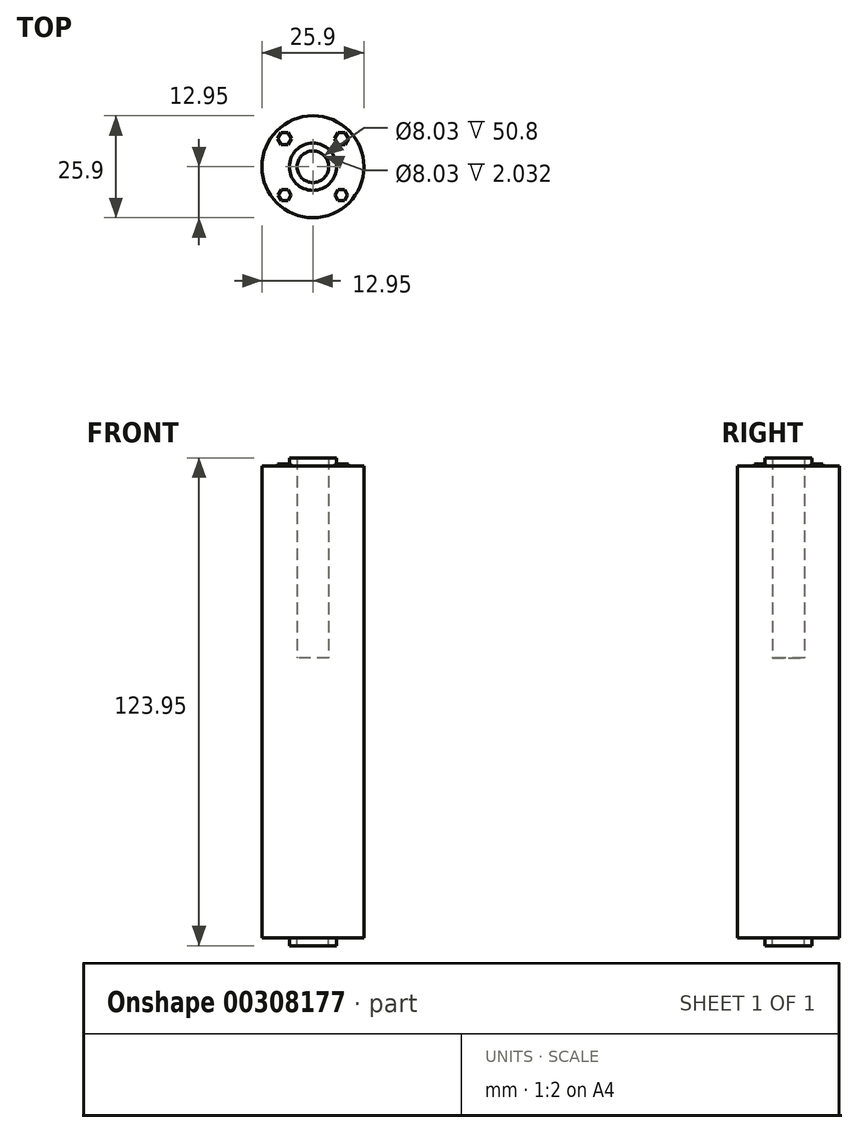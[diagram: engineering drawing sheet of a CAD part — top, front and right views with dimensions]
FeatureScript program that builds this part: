
annotation { "Feature Type Name" : "Feature", "Feature Type Description" : "" }
export const myFeature = defineFeature(function(context is Context, id is Id, definition is map)
    precondition{}
    {
        {
            var Q0;
            Q0=qCreatedBy(makeId("Top.planeOp"),FACE);
            var sketch = newSketch(context, id + "F0", { "sketchPlane" : qUnion([Q0])});
            skCircle(sketch, "E0", {"center": v(0, 0) * mm, "radius": 12.95 * mm});
            skCircle(sketch, "E1", {"center": v(0, 0) * mm, "radius": 6 * mm});
            skCircle(sketch, "E2", {"center": v(0, 0) * mm, "radius": 4.01 * mm});
            skSolve(sketch);
        }
        {
            var Q0;
            Q0 = qSketchRegion(id + "F0", true);
            var Q1;
            Q1=makeQuery(id+"F0.imprint","IMPRINT",FACE,{"disambiguationData":[TD([[makeQuery(id+"F0.imprint","IMPRINT",EDGE,{"derivedFrom":sQuery(id+"F0.wireOp",EDGE,"E1")}),1.0]])]});
            var Q2;
            Q2=makeQuery(id+"F0.imprint","IMPRINT",FACE,{"disambiguationData":[TD([[makeQuery(id+"F0.imprint","IMPRINT",EDGE,{"derivedFrom":sQuery(id+"F0.wireOp",EDGE,"E2")}),1.0]])]});
            extrude(context, id + "F1", {"entities" : qUnion([Q0, Q1, Q2]), "depth" : 119.89 * mm});
        }
        {
            var Q0;
            Q0=makeQuery(id+"F1.opExtrude","CAP_FACE",FACE,{"disambiguationData":[OSD([sQuery(id+"F0.wireOp",EDGE,"E0")])],"isStart":false});
            var sketch = newSketch(context, id + "F2", { "sketchPlane" : qUnion([Q0])});
            skCircle(sketch, "E3.0", {"center": v(0, 0) * mm, "radius": 4.01 * mm});
            skCircle(sketch, "E4.0", {"center": v(0, 0) * mm, "radius": 6 * mm});
            skSolve(sketch);
        }
        {
            var Q0;
            Q0=makeQuery(id+"F2.imprint","IMPRINT",FACE,{"disambiguationData":[TD([[makeQuery(id+"F2.imprint","IMPRINT",EDGE,{"derivedFrom":sQuery(id+"F2.wireOp",EDGE,"E3.0")}),-1.0]])]});
            extrude(context, id + "F3", {"entities" : qUnion([Q0]), "operationType" : NewBodyOperationType.ADD, "depth" : 2.03 * mm});
        }
        {
            var Q0;
            Q0=sQuery(id+"F0.wireOp",EDGE,"E2");
            var Q1;
            Q1=sQuery(id+"F0.wireOp",EDGE,"E1");
            extrude(context, id + "F4", {"bodyType" : ToolBodyType.SURFACE, "surfaceEntities" : qUnion([Q0, Q1]), "oppositeDirection" : true, "depth" : 2.03 * mm});
        }
        {
            var Q0;
            Q0=makeQuery(id+"F0.imprint","IMPRINT",FACE,{"disambiguationData":[TD([[makeQuery(id+"F0.imprint","IMPRINT",EDGE,{"derivedFrom":sQuery(id+"F0.wireOp",EDGE,"E2")}),1.0]])]});
            var sketch = newSketch(context, id + "F5", { "sketchPlane" : qUnion([Q0])});
            skCircle(sketch, "E5.0", {"center": v(0, 0) * mm, "radius": 4.01 * mm});
            skCircle(sketch, "E6.0", {"center": v(0, 0) * mm, "radius": 6 * mm});
            skSolve(sketch);
        }
        {
            var Q0;
            Q0 = qSketchRegion(id + "F5", true);
            var Q1;
            Q1=makeQuery(id+"F0.imprint","IMPRINT",FACE,{"disambiguationData":[TD([[makeQuery(id+"F0.imprint","IMPRINT",EDGE,{"derivedFrom":sQuery(id+"F0.wireOp",EDGE,"E1")}),1.0]])]});
            extrude(context, id + "F6", {"entities" : qUnion([Q0, Q1]), "operationType" : NewBodyOperationType.ADD, "oppositeDirection" : true, "depth" : 2.03 * mm});
        }
        {
            var Q0;
            Q0=makeQuery(id+"F3.opExtrude","CAP_FACE",FACE,{"disambiguationData":[OSD([sQuery(id+"F2.wireOp",EDGE,"E3.0"),sQuery(id+"F2.wireOp",EDGE,"E4.0")])],"isStart":false});
            var sketch = newSketch(context, id + "F7", { "sketchPlane" : qUnion([Q0])});
            skCircle(sketch, "E7.cCircle", {"center": v(0, 0) * mm, "radius": 6.99 * mm, "construction": true});
            skLineSegment(sketch, "E7.0", {"start": v(6.99, 6.99) * mm, "end": v(6.99, -6.99) * mm});
            skLineSegment(sketch, "E7.1", {"start": v(6.99, -6.99) * mm, "end": v(-6.99, -6.99) * mm});
            skLineSegment(sketch, "E7.2", {"start": v(-6.99, -6.99) * mm, "end": v(-6.99, 6.99) * mm});
            skLineSegment(sketch, "E7.3", {"start": v(-6.99, 6.99) * mm, "end": v(6.99, 6.99) * mm});
            skPoint(sketch, "E7.0.midPoint", {"position": v(6.99, 0) * mm});
            skCircle(sketch, "E8", {"center": v(6.99, 6.99) * mm, "radius": 1.9 * mm});
            skCircle(sketch, "E9", {"center": v(-6.99, 6.99) * mm, "radius": 2.13 * mm});
            skCircle(sketch, "E10", {"center": v(-6.99, -6.99) * mm, "radius": 2.24 * mm});
            skCircle(sketch, "E11", {"center": v(6.99, -6.99) * mm, "radius": 1.74 * mm});
            skSolve(sketch);
        }
        {
            var Q0;
            Q0=makeQuery(id+"F7.imprint","IMPRINT",FACE,{"disambiguationData":[TD([[makeQuery(id+"F7.imprint","IMPRINT",EDGE,{"derivedFrom":makeQuery(id+"F3.opExtrude","CAP_EDGE",EDGE,{"disambiguationData":[OSD([sQuery(id+"F2.wireOp",EDGE,"E3.0")])],"isStart":false})}),1.0]])]});
            extrude(context, id + "F8", {"entities" : qUnion([Q0]), "operationType" : NewBodyOperationType.REMOVE, "oppositeDirection" : true, "depth" : 50.8 * mm});
        }
        {
            var Q0;
            {var subQ0=sQuery(id+"F0.wireOp",EDGE,"E0");Q0=makeQuery(id+"F3.boolean.opBoolean","SPLIT",FACE,{"disambiguationData":[TD([makeQuery(id+"F1.opExtrude","SWEPT_FACE",FACE,{"disambiguationData":[OSD([subQ0])]})])],"derivedFrom":makeQuery(id+"F1.opExtrude","CAP_FACE",FACE,{"disambiguationData":[OSD([subQ0])],"isStart":false})});}
            var sketch = newSketch(context, id + "F9", { "sketchPlane" : qUnion([Q0])});
            skCircle(sketch, "E12.cCircle", {"center": v(0, 0) * mm, "radius": 7.2 * mm, "construction": true});
            skLineSegment(sketch, "E12.0", {"start": v(7.2, -7.2) * mm, "end": v(-7.2, -7.2) * mm});
            skLineSegment(sketch, "E12.1", {"start": v(-7.2, -7.2) * mm, "end": v(-7.2, 7.2) * mm});
            skLineSegment(sketch, "E12.2", {"start": v(-7.2, 7.2) * mm, "end": v(7.2, 7.2) * mm});
            skLineSegment(sketch, "E12.3", {"start": v(7.2, 7.2) * mm, "end": v(7.2, -7.2) * mm});
            skPoint(sketch, "E12.0.midPoint", {"position": v(0, -7.2) * mm});
            skCircle(sketch, "E13.cCircle", {"center": v(-7.2, 7.2) * mm, "radius": 1.54 * mm, "construction": true});
            skLineSegment(sketch, "E13.0", {"start": v(-6.31, 5.66) * mm, "end": v(-8.1, 5.66) * mm});
            skLineSegment(sketch, "E13.1", {"start": v(-8.1, 5.66) * mm, "end": v(-8.99, 7.2) * mm});
            skLineSegment(sketch, "E13.2", {"start": v(-8.99, 7.2) * mm, "end": v(-8.1, 8.75) * mm});
            skLineSegment(sketch, "E13.3", {"start": v(-8.1, 8.75) * mm, "end": v(-6.31, 8.75) * mm});
            skLineSegment(sketch, "E13.4", {"start": v(-6.31, 8.75) * mm, "end": v(-5.42, 7.2) * mm});
            skLineSegment(sketch, "E13.5", {"start": v(-5.42, 7.2) * mm, "end": v(-6.31, 5.66) * mm});
            skPoint(sketch, "E13.0.midPoint", {"position": v(-7.2, 5.66) * mm});
            skCircle(sketch, "E14.cCircle", {"center": v(7.2, 7.2) * mm, "radius": 1.54 * mm, "construction": true});
            skLineSegment(sketch, "E14.0", {"start": v(8.1, 5.66) * mm, "end": v(6.31, 5.66) * mm});
            skLineSegment(sketch, "E14.1", {"start": v(6.31, 5.66) * mm, "end": v(5.42, 7.2) * mm});
            skLineSegment(sketch, "E14.2", {"start": v(5.42, 7.2) * mm, "end": v(6.31, 8.75) * mm});
            skLineSegment(sketch, "E14.3", {"start": v(6.31, 8.75) * mm, "end": v(8.1, 8.75) * mm});
            skLineSegment(sketch, "E14.4", {"start": v(8.1, 8.75) * mm, "end": v(8.99, 7.2) * mm});
            skLineSegment(sketch, "E14.5", {"start": v(8.99, 7.2) * mm, "end": v(8.1, 5.66) * mm});
            skPoint(sketch, "E14.0.midPoint", {"position": v(7.2, 5.66) * mm});
            skCircle(sketch, "E15.cCircle", {"center": v(-7.2, -7.2) * mm, "radius": 1.41 * mm, "construction": true});
            skLineSegment(sketch, "E15.0", {"start": v(-8.02, -5.8) * mm, "end": v(-6.39, -5.8) * mm});
            skLineSegment(sketch, "E15.1", {"start": v(-6.39, -5.8) * mm, "end": v(-5.57, -7.2) * mm});
            skLineSegment(sketch, "E15.2", {"start": v(-5.57, -7.2) * mm, "end": v(-6.39, -8.62) * mm});
            skLineSegment(sketch, "E15.3", {"start": v(-6.39, -8.62) * mm, "end": v(-8.02, -8.62) * mm});
            skLineSegment(sketch, "E15.4", {"start": v(-8.02, -8.62) * mm, "end": v(-8.84, -7.2) * mm});
            skLineSegment(sketch, "E15.5", {"start": v(-8.84, -7.2) * mm, "end": v(-8.02, -5.8) * mm});
            skPoint(sketch, "E15.0.midPoint", {"position": v(-7.2, -5.8) * mm});
            skCircle(sketch, "E16.cCircle", {"center": v(7.2, -7.2) * mm, "radius": 1.41 * mm, "construction": true});
            skLineSegment(sketch, "E16.0", {"start": v(6.39, -5.8) * mm, "end": v(8.02, -5.8) * mm});
            skLineSegment(sketch, "E16.1", {"start": v(8.02, -5.8) * mm, "end": v(8.84, -7.2) * mm});
            skLineSegment(sketch, "E16.2", {"start": v(8.84, -7.2) * mm, "end": v(8.02, -8.62) * mm});
            skLineSegment(sketch, "E16.3", {"start": v(8.02, -8.62) * mm, "end": v(6.39, -8.62) * mm});
            skLineSegment(sketch, "E16.4", {"start": v(6.39, -8.62) * mm, "end": v(5.57, -7.2) * mm});
            skLineSegment(sketch, "E16.5", {"start": v(5.57, -7.2) * mm, "end": v(6.39, -5.8) * mm});
            skPoint(sketch, "E16.0.midPoint", {"position": v(7.2, -5.8) * mm});
            skSolve(sketch);
        }
        {
            var Q0;
            {var subQ3=sQuery(id+"F9.wireOp",EDGE,"E16.5");Q0=makeQuery(id+"F9.imprint","IMPRINT",FACE,{"disambiguationData":[TD([[makeQuery(id+"F9.imprint","IMPRINT",EDGE,{"derivedFrom":subQ3}),-1.0]])]});}
            var Q1;
            {var subQ0=sQuery(id+"F9.wireOp",EDGE,"E16.1");Q1=makeQuery(id+"F9.imprint","IMPRINT",FACE,{"disambiguationData":[TD([[makeQuery(id+"F9.imprint","IMPRINT",EDGE,{"derivedFrom":subQ0}),-1.0]])]});}
            var Q2;
            {var subQ0=sQuery(id+"F9.wireOp",EDGE,"E15.2");Q2=makeQuery(id+"F9.imprint","IMPRINT",FACE,{"disambiguationData":[TD([[makeQuery(id+"F9.imprint","IMPRINT",EDGE,{"derivedFrom":subQ0}),-1.0]])]});}
            var Q3;
            {var subQ3=sQuery(id+"F9.wireOp",EDGE,"E15.1");Q3=makeQuery(id+"F9.imprint","IMPRINT",FACE,{"disambiguationData":[TD([[makeQuery(id+"F9.imprint","IMPRINT",EDGE,{"derivedFrom":subQ3}),-1.0]])]});}
            var Q4;
            {var subQ5=sQuery(id+"F9.wireOp",EDGE,"E13.5");Q4=makeQuery(id+"F9.imprint","IMPRINT",FACE,{"disambiguationData":[TD([[makeQuery(id+"F9.imprint","IMPRINT",EDGE,{"derivedFrom":subQ5}),-1.0]])]});}
            var Q5;
            {var subQ0=sQuery(id+"F9.wireOp",EDGE,"E13.1");Q5=makeQuery(id+"F9.imprint","IMPRINT",FACE,{"disambiguationData":[TD([[makeQuery(id+"F9.imprint","IMPRINT",EDGE,{"derivedFrom":subQ0}),-1.0]])]});}
            var Q6;
            {var subQ0=sQuery(id+"F9.wireOp",EDGE,"E14.2");Q6=makeQuery(id+"F9.imprint","IMPRINT",FACE,{"disambiguationData":[TD([[makeQuery(id+"F9.imprint","IMPRINT",EDGE,{"derivedFrom":subQ0}),-1.0]])]});}
            var Q7;
            {var subQ3=sQuery(id+"F9.wireOp",EDGE,"E14.1");Q7=makeQuery(id+"F9.imprint","IMPRINT",FACE,{"disambiguationData":[TD([[makeQuery(id+"F9.imprint","IMPRINT",EDGE,{"derivedFrom":subQ3}),-1.0]])]});}
            extrude(context, id + "F10", {"entities" : qUnion([Q0, Q1, Q2, Q3, Q4, Q5, Q6, Q7]), "operationType" : NewBodyOperationType.ADD, "depth" : 0.5 * mm});
        }
    });
